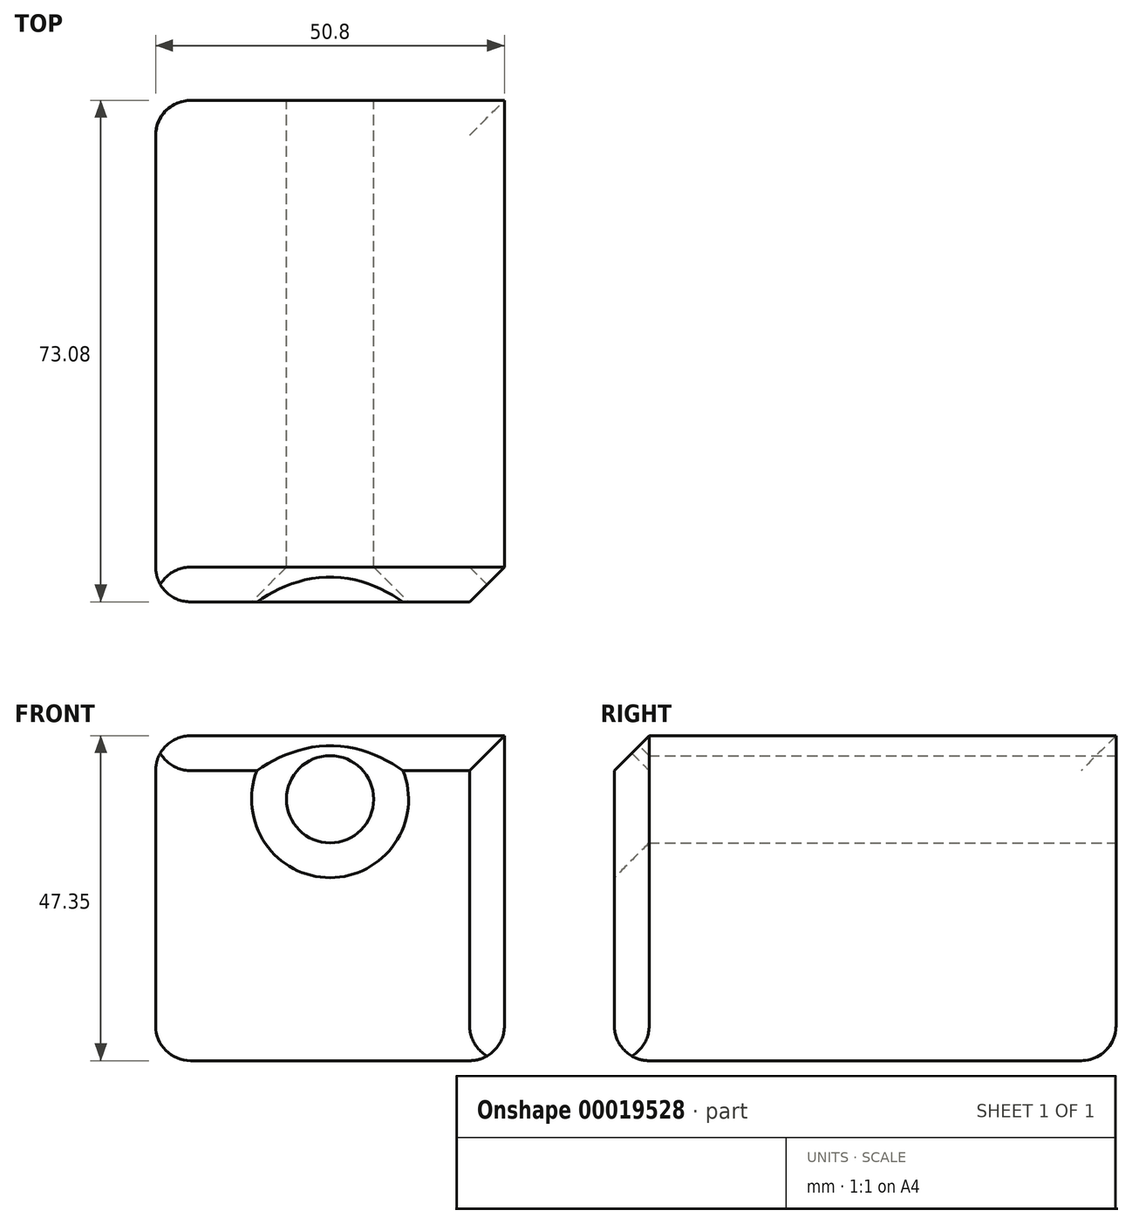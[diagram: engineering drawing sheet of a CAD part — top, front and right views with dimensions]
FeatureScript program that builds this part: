
annotation { "Feature Type Name" : "Feature", "Feature Type Description" : "" }
export const myFeature = defineFeature(function(context is Context, id is Id, definition is map)
    precondition{}
    {
        {
            var Q0;
            Q0=qCreatedBy(makeId("Front.planeOp"),FACE);
            var sketch = newSketch(context, id + "F0", { "sketchPlane" : qUnion([Q0])});
            skLineSegment(sketch, "E0.bottom", {"start": v(-25.4, 9.25) * mm, "end": v(25.4, 9.25) * mm});
            skLineSegment(sketch, "E0.top", {"start": v(-25.4, -38.1) * mm, "end": v(25.4, -38.1) * mm});
            skLineSegment(sketch, "E0.left", {"start": v(-25.4, 9.25) * mm, "end": v(-25.4, -38.1) * mm});
            skLineSegment(sketch, "E0.right", {"start": v(25.4, 9.25) * mm, "end": v(25.4, -38.1) * mm});
            skCircle(sketch, "E1", {"center": v(0, 0) * mm, "radius": 6.35 * mm});
            skSolve(sketch);
        }
        {
            var Q0;
            Q0=makeQuery(id+"F0.imprint","IMPRINT",FACE,{"disambiguationData":[TD([[makeQuery(id+"F0.imprint","IMPRINT",EDGE,{"derivedFrom":sQuery(id+"F0.wireOp",EDGE,"E0.bottom")}),-1.0]])]});
            extrude(context, id + "F1", {"entities" : qUnion([Q0]), "depth" : 73.08 * mm});
        }
        {
            var Q0;
            Q0=makeQuery(id+"F1.opExtrude","SWEPT_FACE",FACE,{"disambiguationData":[OSD([sQuery(id+"F0.wireOp",EDGE,"E0.left")])]});
            var Q1;
            Q1=makeQuery(id+"F1.opExtrude","SWEPT_FACE",FACE,{"disambiguationData":[OSD([sQuery(id+"F0.wireOp",EDGE,"E0.top")])]});
            fillet(context, id + "F2", {"entities" : qUnion([Q0, Q1]), "radius" : 5.08 * mm, "tangentPropagation" : true, "allowEdgeOverflow" : false});
        }
        {
            var Q0;
            Q0=makeQuery(id+"F1.opExtrude","CAP_FACE",FACE,{"disambiguationData":[OSD([sQuery(id+"F0.wireOp",EDGE,"E0.bottom"),sQuery(id+"F0.wireOp",EDGE,"E0.top"),sQuery(id+"F0.wireOp",EDGE,"E0.left"),sQuery(id+"F0.wireOp",EDGE,"E0.right"),sQuery(id+"F0.wireOp",EDGE,"E1")])],"isStart":false});
            chamfer(context, id + "F3", {"entities" : qUnion([Q0]), "width" : 5.08 * mm, "tangentPropagation" : true});
        }
    });
